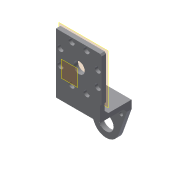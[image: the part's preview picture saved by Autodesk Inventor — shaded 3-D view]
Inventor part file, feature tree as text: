
AUTODESK INVENTOR PART (.ipt)
format: ipt  version: 2019.4 (Build 234330000, 330)  size: 192,000 bytes
history: native  units: mm
features: sketch x5, extrude x4, projected_geometry x4, other x4, plane x2, hole x2, reference x2, chamfer x1
ambient origin geometry x8: Origin, YZ Plane, XZ Plane, XY Plane, X Axis, Y Axis, Z Axis, Center Point
bodies: Solid1 (feature_tree)
feature tree (24):
  plane  "Work Plane1"
  extrude  "Extrusion1"  Depth=6.0mm TaperAngle=0.0deg
  plane  "Work Plane3"
  hole  "Hole1"  [1 undecoded]
  extrude  "Extrusion9"  Depth=6.0mm
  extrude  "Extrusion10"  TaperAngle=90.0deg  [1 undecoded]
  chamfer  "Chamfer3"  Distance=30.0mm
  hole  "Hole2"  [1 undecoded]
  extrude  "Extrusion11"  Depth=10.0mm
  sketch  "Sketch1"  dims[d0=3.0mm d1=6.0mm d2=0.0mm]
  reference  "Reference1"
  reference  "Reference2"
  sketch  "Sketch10"  dims[d31=3.2mm d32=6.0mm d33=8.0mm d34=4.0mm d35=90.0deg d36=8.0mm d37=20.594885mm d55=20.0mm]
  projected_geometry  "Projected Loop7"
  sketch  "Sketch11"  dims[d56=90.0deg d57=6.0mm]
  projected_geometry  "Projected Loop8"
  sketch  "Sketch12"  dims[d58=90.0deg d59=90.0deg]
  projected_geometry  "Projected Loop9"
  sketch  "Sketch13"  dims[d60=90.0deg d61=30.0mm d63=10.0mm d64=0.0mm d65=20.0mm d66=10.0mm d67=0.0mm d68=5.0mm d69=2.0mm d70=45.0deg d71=6.0mm d72=40.0mm d73=40.0mm d74=4.9mm d75=6.0mm d76=8.0mm d77=4.0mm d78=90.0deg d79=8.0mm d80=20.594885mm d81=35.0mm d82=10.0mm d83=0.0mm]
  projected_geometry  "Projected Loop10"
  other  "Application_Fluorescence_Microscope_Infinity_cellstorm_v3.iam"
  other  "00_XY_stage-CHUO_SEIKI_LD-647-R1:1"
  other  "00_XY_stage-CHUO_SEIKI_LD-647-R1-Top:1"
  other  "00_Microscope_Objective:1"
note: 3 required parameter values undecoded (feature->parameter linkage not recoverable at this tier; creation-order binding heuristic only, values carry confidence <= 0.55)
